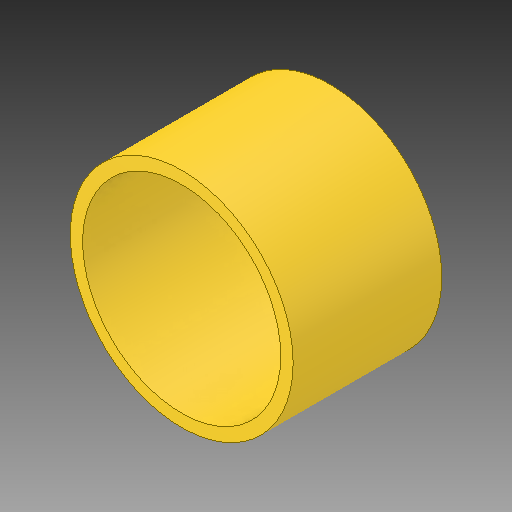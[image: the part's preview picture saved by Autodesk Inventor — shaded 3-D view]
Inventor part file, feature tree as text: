
AUTODESK INVENTOR PART (.ipt)
format: ipt  version: 2019.4 (Build 234330000, 330)  size: 113,152 bytes
history: native  units: mm
features: extrude x1, sketch x1
ambient origin geometry x8: Origin, YZ Plane, XZ Plane, XY Plane, X Axis, Y Axis, Z Axis, Center Point
bodies: Solid1 (feature_tree)
feature tree (2):
  extrude  "Extrusion1"  Depth=6.0mm
  sketch  "Sketch1"  dims[d0=8.0mm d1=9.0mm d2=6.0mm d3=0.0mm]
